# Revit family: 44729503
name_source: partatom
category: Plumbing Fixtures
revit_build: Autodesk Revit 2016 (Build: 20150220_1215(x64)
units: mm (PartAtom-declared; Revit-internal decimal feet)

## family parameters
Always vertical = Yes
Cut with Voids When Loaded = No
OmniClass Number = 23.45.55.00
OmniClass Title = Sanitary Faucets, Wastes
Part Type = Normal
Room Calculation Point = No
Round Connector Dimension = Use Diameter
Shared = No
Work Plane-Based = No

## types (1)
- 44729503 Cover part for bath and shower faucet, 230/12 V
    2D/3D/BIM Files URL = http://static.hansa.com
    Advanced Features = Rosette without screws
    AssetType = Fixed
    BIMObjectName = 44729503
    BodyMaterial = Brass
    Brand = Hansa
    Catalog Drawing URL = http://static.hansa.com
    Category = Bathroom, shower
    Class = Fixed connection
    CloseOffRating = 0
    Color = Chrome
    ConvergoRefNr = 0087-1809-0029-FI
    Customs Code = 84819000
    DN Size = DN15
    Dimension Drawing URL = http://static.hansa.com
    DurationUnit = Year
    EAN Number = 4015474277915
    EMC Directive = 2004/108/EY
    Electrical Connection = 230 / 12 V
    Electronic Parts = Control unit
    Extensions = EcoLed press pad;Tiptronic flex
    FDV Document URL = http://www.hansa.com
    FaucetMainMaterial = Brass
    Features = Fixed connection
    Filling Time = 10 min (0 - 20 min)
    Finish = Polished
    FlowCoefficient = 0
    Group = Bath and shower faucets
    IfcExportAs = IfcValveType
    IfcExportType = FAUCET
    Included = Rosette plate frame, square wall rosette, sleeve
    Installation Type = Wall-mounted concealed
    Installation and Maintenance = http://static.hansa.com
    Lever Handle = Temperature control handle
    ManufacterURL = http://www.hansa.com
    Manufacturer = Hansa
    ManufacturerName = Hansa
    Market = AUT;BEL;CZE;DEU;ESP;FRA;INT;ITA;NLD;SVK
    Material = Brass
    Max Flow Period = 480.0 s
    Max. Hot Water Supply = 70 °C
    Model = 44729503 Cover part for bath and shower faucet, 230/12 V
    NBSDescription = Water supply fittings for baths
    NBSReference = 45-35-70/315
    Name = 44729503 Cover part for bath and shower faucet, 230/12 V
    Name_en = 44729503 Cover part for bath and shower faucet, 230/12 V
    NominalDepth = 68 mm
    NominalHeight = 75 mm
    NominalWidth = 275 mm
    Operating Voltage = 12 V
    Package Weight = 2.17 kg
    Package external Dimensions = 490 x 145 x 55
    Product Code = 44729503
    Product Datasheet = http://www.hansa.com
    Product Family = HANSAMATRIX
    Product Image URL = http://static.hansa.com
    Product URL = http://static.hansa.com
    Protection Class = IP 55 / transformer IP 40
    Revision = 2
    Shape = Sculptured
    Size = 275x68x75 mm
    Spare Parts = http://static.hansa.com
    Technology Sales Arguments = The right product for the modular and design-oriented concealed installation system HANSAMATRIX.
    Temperature = Thermostatic safety stop at 38°C
    Uniclass2 = Pr_40_30_96_07
    Uniclass2015Description = Bath manual water supply sets
    Uniclass2015Reference = Pr_40_20_87_07
    Version = 2
    VersionDate = 01/01/2019
    WarrantyDescription = http://warranty.hansa.com
    WarrantyDurationUnit = Year
    WorkingPressure = 100 - 1000 kPa

## geometry (parser evidence)
native form markers: Sweep x5
no freeform markers — native parametric forms only
